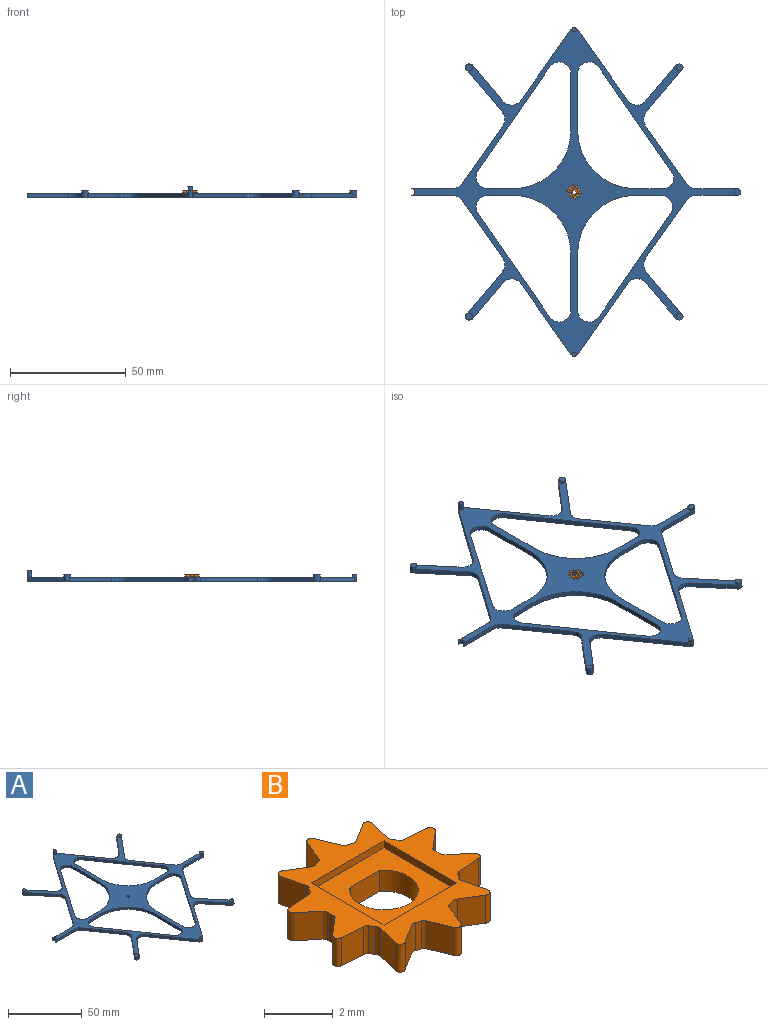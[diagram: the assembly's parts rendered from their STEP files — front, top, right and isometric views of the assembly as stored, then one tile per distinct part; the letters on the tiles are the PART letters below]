
ASSEMBLY  parts=2 mates=1
PART A: 82 faces, bbox 142.5x142.4x5 mm
  f0: plane 2x0.19mm, normal (-0.65,0.76,0), area 0.5mm2, adj f65,f66,f67,f77
  f1: plane 18.27x15.44mm, normal (-0.76,-0.65,0), area 47.8mm2, adj f2,f66,f67,f77
  f2: cylinder r=5mm len=6.11mm, axis (0,0,-1), area 13.2mm2, adj f1,f3,f66,f67
  f3: plane 24.88x17.57mm, normal (-0.82,0.58,0), area 60.9mm2, adj f2,f4,f66,f67
  f4: cylinder r=5mm len=4.08mm, axis (0,0,-1), area 9.6mm2, adj f3,f5,f66,f67
  f5: plane 17.91x2mm, normal (0,1,0), area 35.8mm2, adj f4,f6,f66,f67
  f6: cylinder r=1.5mm len=3mm, axis (0,0,-1), area 9.4mm2, adj f5,f7,f66,f67
  f7: plane 17.91x2mm, normal (0,-1,0), area 35.8mm2, adj f6,f8,f66,f67
  f8: cylinder r=5mm len=4.08mm, axis (0,0,-1), area 9.6mm2, adj f7,f9,f66,f67
  f9: plane 24.88x17.57mm, normal (-0.82,-0.58,0), area 60.9mm2, adj f8,f10,f66,f67
  f10: cylinder r=5mm len=6.11mm, axis (0,0,-1), area 13.2mm2, adj f9,f11,f66,f67
  f11: plane 18.27x15.44mm, normal (-0.76,0.65,0), area 47.8mm2, adj f10,f66,f67,f79
  f12: plane 2x0.19mm, normal (-0.65,-0.76,0), area 0.5mm2, adj f13,f66,f67,f79
  f13: plane 15.64x13.22mm, normal (0.76,-0.65,0), area 41mm2, adj f12,f14,f66,f67
  f14: cylinder r=5mm len=7.9mm, axis (0,0,-1), area 18.3mm2, adj f13,f15,f66,f67
  f15: plane 30.52x21.54mm, normal (-0.82,-0.58,0), area 74.7mm2, adj f14,f16,f66,f67
  f16: plane 2x0.5mm, normal (0,-1,0), area 1mm2, adj f15,f66,f67,f68
  f17: plane 2x0.5mm, normal (0,-1,0), area 1mm2, adj f18,f66,f67,f68
  f18: plane 30.73x21.69mm, normal (0.82,-0.58,0), area 75.2mm2, adj f17,f19,f66,f67
  f19: cylinder r=4.8mm len=7.59mm, axis (0,0,-1), area 17.5mm2, adj f18,f20,f66,f67
  f20: plane 15.84x13.38mm, normal (-0.76,-0.65,0), area 41.5mm2, adj f19,f21,f66,f67
  f21: plane 2x0.19mm, normal (0.65,-0.76,0), area 0.5mm2, adj f20,f66,f67,f75
  f22: plane 18.27x15.44mm, normal (0.76,0.65,0), area 47.8mm2, adj f23,f66,f67,f75
  f23: cylinder r=5mm len=6.11mm, axis (0,0,-1), area 13.2mm2, adj f22,f24,f66,f67
  f24: plane 24.88x17.57mm, normal (0.82,-0.58,0), area 60.9mm2, adj f23,f25,f66,f67
  f25: cylinder r=5mm len=4.08mm, axis (0,0,-1), area 9.6mm2, adj f24,f26,f66,f67
  f26: plane 17.91x2mm, normal (0,-1,0), area 35.8mm2, adj f25,f66,f67,f71
  f27: plane 17.91x2mm, normal (0,1,0), area 35.8mm2, adj f28,f66,f67,f71
  f28: cylinder r=5mm len=4.08mm, axis (0,0,-1), area 9.6mm2, adj f27,f29,f66,f67
  f29: plane 24.88x17.57mm, normal (0.82,0.58,0), area 60.9mm2, adj f28,f30,f66,f67
  f30: cylinder r=5mm len=6.11mm, axis (0,0,-1), area 13.2mm2, adj f29,f31,f66,f67
  f31: plane 18.27x15.44mm, normal (0.76,-0.65,0), area 47.8mm2, adj f30,f66,f67,f73
  f32: plane 2x0.19mm, normal (0.65,0.76,0), area 0.5mm2, adj f33,f66,f67,f73
  f33: plane 15.64x13.22mm, normal (-0.76,0.65,0), area 41mm2, adj f32,f34,f66,f67
  f34: cylinder r=5mm len=7.9mm, axis (0,0,-1), area 18.3mm2, adj f33,f35,f66,f67
  f35: plane 30.52x21.54mm, normal (0.82,0.58,0), area 74.7mm2, adj f34,f36,f66,f67
  f36: plane 2x0.5mm, normal (0,1,0), area 1mm2, adj f35,f66,f67,f70
  f37: plane 2x0.5mm, normal (0,1,0), area 1mm2, adj f38,f66,f67,f70
  f38: plane 30.52x21.54mm, normal (-0.82,0.58,0), area 74.7mm2, adj f37,f39,f66,f67
  f39: cylinder r=5mm len=7.9mm, axis (0,0,-1), area 18.3mm2, adj f38,f65,f66,f67
  f40: cylinder r=5mm len=7.85mm, axis (0,0,-1), area 21.8mm2, adj f41,f60,f66,f67
  f41: plane 44.7x30.96mm, normal (-0.82,0.57,0), area 108.7mm2, adj f40,f42,f66,f67
  f42: cylinder r=5mm len=9.11mm, axis (0,0,-1), area 25.4mm2, adj f41,f43,f66,f67
  f43: plane 24.7x2mm, normal (1,0,0), area 49.4mm2, adj f42,f44,f66,f67
  f44: cylinder r=25mm len=25mm, axis (0,0,-1), area 78.5mm2, adj f43,f60,f66,f67
  f45: cylinder r=5mm len=7.85mm, axis (0,0,-1), area 21.8mm2, adj f46,f61,f66,f67
  f46: plane 10.96x2mm, normal (0,-1,0), area 21.9mm2, adj f45,f47,f66,f67
  f47: cylinder r=25mm len=25mm, axis (0,0,-1), area 78.5mm2, adj f46,f48,f66,f67
  f48: plane 24.7x2mm, normal (-1,0,0), area 49.4mm2, adj f47,f49,f66,f67
  f49: cylinder r=5mm len=9.11mm, axis (0,0,-1), area 25.4mm2, adj f48,f61,f66,f67
  f50: cylinder r=5mm len=7.85mm, axis (0,0,-1), area 21.8mm2, adj f51,f62,f66,f67
  f51: plane 44.7x30.96mm, normal (0.82,-0.57,0), area 108.7mm2, adj f50,f52,f66,f67
  f52: cylinder r=5mm len=9.11mm, axis (0,0,-1), area 25.4mm2, adj f51,f53,f66,f67
  f53: plane 24.7x2mm, normal (-1,0,0), area 49.4mm2, adj f52,f54,f66,f67
  f54: cylinder r=25mm len=25mm, axis (0,0,-1), area 78.5mm2, adj f53,f62,f66,f67
  f55: cylinder r=4.43mm len=6.95mm, axis (0,0,-1), area 19.3mm2, adj f56,f63,f66,f67
  f56: plane 12.05x2mm, normal (0,1,0), area 24.1mm2, adj f55,f57,f66,f67
  f57: cylinder r=25mm len=25mm, axis (0,0,-1), area 78.5mm2, adj f56,f58,f66,f67
  f58: plane 24.7x2mm, normal (1,0,0), area 49.4mm2, adj f57,f59,f66,f67
  f59: cylinder r=5mm len=9.11mm, axis (0,0,-1), area 25.4mm2, adj f58,f63,f66,f67
  f60: plane 10.96x2mm, normal (0,-1,0), area 21.9mm2, adj f40,f44,f66,f67
  f61: plane 44.7x30.96mm, normal (0.82,0.57,0), area 108.7mm2, adj f45,f49,f66,f67
  f62: plane 10.96x2mm, normal (0,1,0), area 21.9mm2, adj f50,f54,f66,f67
  f63: plane 45.6x31.58mm, normal (-0.82,-0.57,0), area 110.9mm2, adj f55,f59,f66,f67
  f64: cylinder r=1mm len=2mm, axis (0,0,-1), area 12.6mm2, adj f66,f67
  f65: plane 15.64x13.22mm, normal (0.76,0.65,0), area 41mm2, adj f0,f39,f66,f67
  f66: plane 141x140.4mm, normal (0,0,1), area 2708.9mm2, adj f0,f1,f2,f3,f4,f5,f6,f7
  f67: plane 142.5x142.4mm, normal (0,0,-1), area 2750.6mm2, adj f0,f1,f2,f3,f4,f5,f6,f7
  f68: cylinder r=1mm len=3mm, axis (0,0,-1), area 12.6mm2, adj f16,f17,f66,f67,f69
  f69: plane 2x2mm, normal (0,0,1), area 3.1mm2, adj f68
  f70: cylinder r=1mm len=5mm, axis (0,0,-1), area 25.1mm2, adj f36,f37,f66,f67,f81
  f71: cylinder r=1.5mm len=3mm, axis (0,0,-1), area 18.8mm2, adj f26,f27,f66,f67,f72
  f72: plane 3x3mm, normal (0,0,1), area 7.1mm2, adj f71
  f73: cylinder r=1.5mm len=3mm, axis (0,0,-1), area 18.8mm2, adj f31,f32,f66,f67,f74
  f74: plane 3x3mm, normal (0,0,1), area 7.1mm2, adj f73
  f75: cylinder r=1.5mm len=3mm, axis (0,0,-1), area 18.8mm2, adj f21,f22,f66,f67,f76
  f76: plane 3x3mm, normal (0,0,1), area 7.1mm2, adj f75
  f77: cylinder r=1.5mm len=3mm, axis (0,0,-1), area 18.8mm2, adj f0,f1,f66,f67,f78
  f78: plane 3x3mm, normal (0,0,1), area 7.1mm2, adj f77
  f79: cylinder r=1.5mm len=3mm, axis (0,0,-1), area 18.8mm2, adj f11,f12,f66,f67,f80
  f80: plane 3x3mm, normal (0,0,1), area 7.1mm2, adj f79
  f81: plane 2x2mm, normal (0,0,1), area 3.1mm2, adj f70
PART B: 69 faces, bbox 6x6.3x1 mm
  f0: plane 1.2x0.75mm, normal (0,-1,0), area 0.9mm2, adj f1,f63,f68
  f1: cylinder r=1mm len=2mm, axis (0,0,-1), area 3.7mm2, adj f0,f63,f68
  f2: plane 6.25x5.96mm, normal (0,0,1), area 11.8mm2, adj f3,f4,f5,f6,f7,f8,f9,f10
  f3: cylinder r=2.2mm len=1mm, axis (0,0,-1), area 0.2mm2, adj f2,f6,f58,f63
  f4: cylinder r=0.15mm len=1mm, axis (0,0,-1), area 0.4mm2, adj f2,f5,f7,f63
  f5: plane 1x0.73mm, normal (-0.53,0.85,0), area 0.9mm2, adj f2,f4,f6,f63
  f6: cylinder r=0.2mm len=1mm, axis (0,0,-1), area 0.2mm2, adj f2,f3,f5,f63
  f7: plane 1x0.83mm, normal (0.97,-0.24,0), area 0.9mm2, adj f2,f4,f8,f63
  f8: cylinder r=0.2mm len=1mm, axis (0,0,-1), area 0.2mm2, adj f2,f7,f9,f63
  f9: cylinder r=2.2mm len=1mm, axis (0,0,-1), area 0.2mm2, adj f2,f8,f12,f63
  f10: cylinder r=0.15mm len=1mm, axis (0,0,-1), area 0.4mm2, adj f2,f11,f13,f63
  f11: plane 1x0.85mm, normal (0.07,1,0), area 0.9mm2, adj f2,f10,f12,f63
  f12: cylinder r=0.2mm len=1mm, axis (0,0,-1), area 0.2mm2, adj f2,f9,f11,f63
  f13: plane 1x0.65mm, normal (0.65,-0.76,0), area 0.9mm2, adj f2,f10,f14,f63
  f14: cylinder r=0.2mm len=1mm, axis (0,0,-1), area 0.2mm2, adj f2,f13,f15,f63
  f15: cylinder r=2.2mm len=1mm, axis (0,0,-1), area 0.2mm2, adj f2,f14,f18,f63
  f16: cylinder r=0.15mm len=1mm, axis (0,0,-1), area 0.4mm2, adj f2,f17,f19,f63
  f17: plane 1x0.65mm, normal (0.65,0.76,0), area 0.9mm2, adj f2,f16,f18,f63
  f18: cylinder r=0.2mm len=1mm, axis (0,0,-1), area 0.2mm2, adj f2,f15,f17,f63
  f19: plane 1x0.85mm, normal (0.07,-1,0), area 0.9mm2, adj f2,f16,f20,f63
  f20: cylinder r=0.2mm len=1mm, axis (0,0,-1), area 0.2mm2, adj f2,f19,f21,f63
  f21: cylinder r=2.2mm len=1mm, axis (0,0,-1), area 0.2mm2, adj f2,f20,f24,f63
  f22: cylinder r=0.15mm len=1mm, axis (0,0,-1), area 0.4mm2, adj f2,f23,f25,f63
  f23: plane 1x0.83mm, normal (0.97,0.24,0), area 0.9mm2, adj f2,f22,f24,f63
  f24: cylinder r=0.2mm len=1mm, axis (0,0,-1), area 0.2mm2, adj f2,f21,f23,f63
  f25: plane 1x0.73mm, normal (-0.53,-0.85,0), area 0.9mm2, adj f2,f22,f26,f63
  f26: cylinder r=0.2mm len=1mm, axis (0,0,-1), area 0.2mm2, adj f2,f25,f27,f63
  f27: cylinder r=2.2mm len=1mm, axis (0,0,-1), area 0.2mm2, adj f2,f26,f30,f63
  f28: cylinder r=0.15mm len=1mm, axis (0,0,-1), area 0.4mm2, adj f2,f29,f31,f63
  f29: plane 1x0.79mm, normal (0.93,-0.38,0), area 0.9mm2, adj f2,f28,f30,f63
  f30: cylinder r=0.2mm len=1mm, axis (0,0,-1), area 0.2mm2, adj f2,f27,f29,f63
  f31: plane 1x0.79mm, normal (-0.93,-0.38,0), area 0.9mm2, adj f2,f28,f32,f63
  f32: cylinder r=0.2mm len=1mm, axis (0,0,-1), area 0.2mm2, adj f2,f31,f33,f63
  f33: cylinder r=2.2mm len=1mm, axis (0,0,-1), area 0.2mm2, adj f2,f32,f36,f63
  f34: cylinder r=0.15mm len=1mm, axis (0,0,-1), area 0.4mm2, adj f2,f35,f37,f63
  f35: plane 1x0.73mm, normal (0.53,-0.85,0), area 0.9mm2, adj f2,f34,f36,f63
  f36: cylinder r=0.2mm len=1mm, axis (0,0,-1), area 0.2mm2, adj f2,f33,f35,f63
  f37: plane 1x0.83mm, normal (-0.97,0.24,0), area 0.9mm2, adj f2,f34,f38,f63
  f38: cylinder r=0.2mm len=1mm, axis (0,0,-1), area 0.2mm2, adj f2,f37,f39,f63
  f39: cylinder r=2.2mm len=1mm, axis (0,0,-1), area 0.2mm2, adj f2,f38,f42,f63
  f40: cylinder r=0.15mm len=1mm, axis (0,0,-1), area 0.4mm2, adj f2,f41,f43,f63
  f41: plane 1x0.85mm, normal (-0.07,-1,0), area 0.9mm2, adj f2,f40,f42,f63
  f42: cylinder r=0.2mm len=1mm, axis (0,0,-1), area 0.2mm2, adj f2,f39,f41,f63
  f43: plane 1x0.65mm, normal (-0.65,0.76,0), area 0.9mm2, adj f2,f40,f44,f63
  f44: cylinder r=0.2mm len=1mm, axis (0,0,-1), area 0.2mm2, adj f2,f43,f45,f63
  f45: cylinder r=2.2mm len=1mm, axis (0,0,-1), area 0.2mm2, adj f2,f44,f48,f63
  f46: cylinder r=0.15mm len=1mm, axis (0,0,-1), area 0.4mm2, adj f2,f47,f49,f63
  f47: plane 1x0.65mm, normal (-0.65,-0.76,0), area 0.9mm2, adj f2,f46,f48,f63
  f48: cylinder r=0.2mm len=1mm, axis (0,0,-1), area 0.2mm2, adj f2,f45,f47,f63
  f49: plane 1x0.85mm, normal (-0.07,1,0), area 0.9mm2, adj f2,f46,f50,f63
  f50: cylinder r=0.2mm len=1mm, axis (0,0,-1), area 0.2mm2, adj f2,f49,f51,f63
  f51: cylinder r=2.2mm len=1mm, axis (0,0,-1), area 0.2mm2, adj f2,f50,f54,f63
  f52: cylinder r=0.15mm len=1mm, axis (0,0,-1), area 0.4mm2, adj f2,f53,f55,f63
  f53: plane 1x0.83mm, normal (-0.97,-0.24,0), area 0.9mm2, adj f2,f52,f54,f63
  f54: cylinder r=0.2mm len=1mm, axis (0,0,-1), area 0.2mm2, adj f2,f51,f53,f63
  f55: plane 1x0.73mm, normal (0.53,0.85,0), area 0.9mm2, adj f2,f52,f56,f63
  f56: cylinder r=0.2mm len=1mm, axis (0,0,-1), area 0.2mm2, adj f2,f55,f57,f63
  f57: cylinder r=2.2mm len=1mm, axis (0,0,-1), area 0.2mm2, adj f2,f56,f62,f63
  f58: cylinder r=0.2mm len=1mm, axis (0,0,-1), area 0.2mm2, adj f2,f3,f59,f63
  f59: plane 1x0.79mm, normal (0.93,0.38,0), area 0.9mm2, adj f2,f58,f60,f63
  f60: cylinder r=0.15mm len=1mm, axis (0,0,-1), area 0.4mm2, adj f2,f59,f61,f63
  f61: plane 1x0.79mm, normal (-0.93,0.38,0), area 0.9mm2, adj f2,f60,f62,f63
  f62: cylinder r=0.2mm len=1mm, axis (0,0,-1), area 0.2mm2, adj f2,f57,f61,f63
  f63: plane 6.25x5.96mm, normal (0,0,-1), area 17.8mm2, adj f0,f1,f3,f4,f5,f6,f7,f8
  f64: plane 3x0.25mm, normal (0,1,0), area 0.8mm2, adj f2,f65,f67,f68
  f65: plane 3x0.25mm, normal (-1,0,0), area 0.8mm2, adj f2,f64,f66,f68
  f66: plane 3x0.25mm, normal (0,-1,0), area 0.8mm2, adj f2,f65,f67,f68
  f67: plane 3x0.25mm, normal (1,0,0), area 0.8mm2, adj f2,f64,f66,f68
  f68: plane 3x3mm, normal (0,0,1), area 6mm2, adj f0,f1,f64,f65,f66,f67
PLACE A t=(-0.06,0.34,-0.93)mm fixed
PLACE B rot(axis=(0,0,-1),61.5deg) t=(-0.14,35.45,1.07)mm
MATE revolute B.f1 <-> A.f66  axis (0,0,-1) through (-0.14,35.45,1.07)mm
